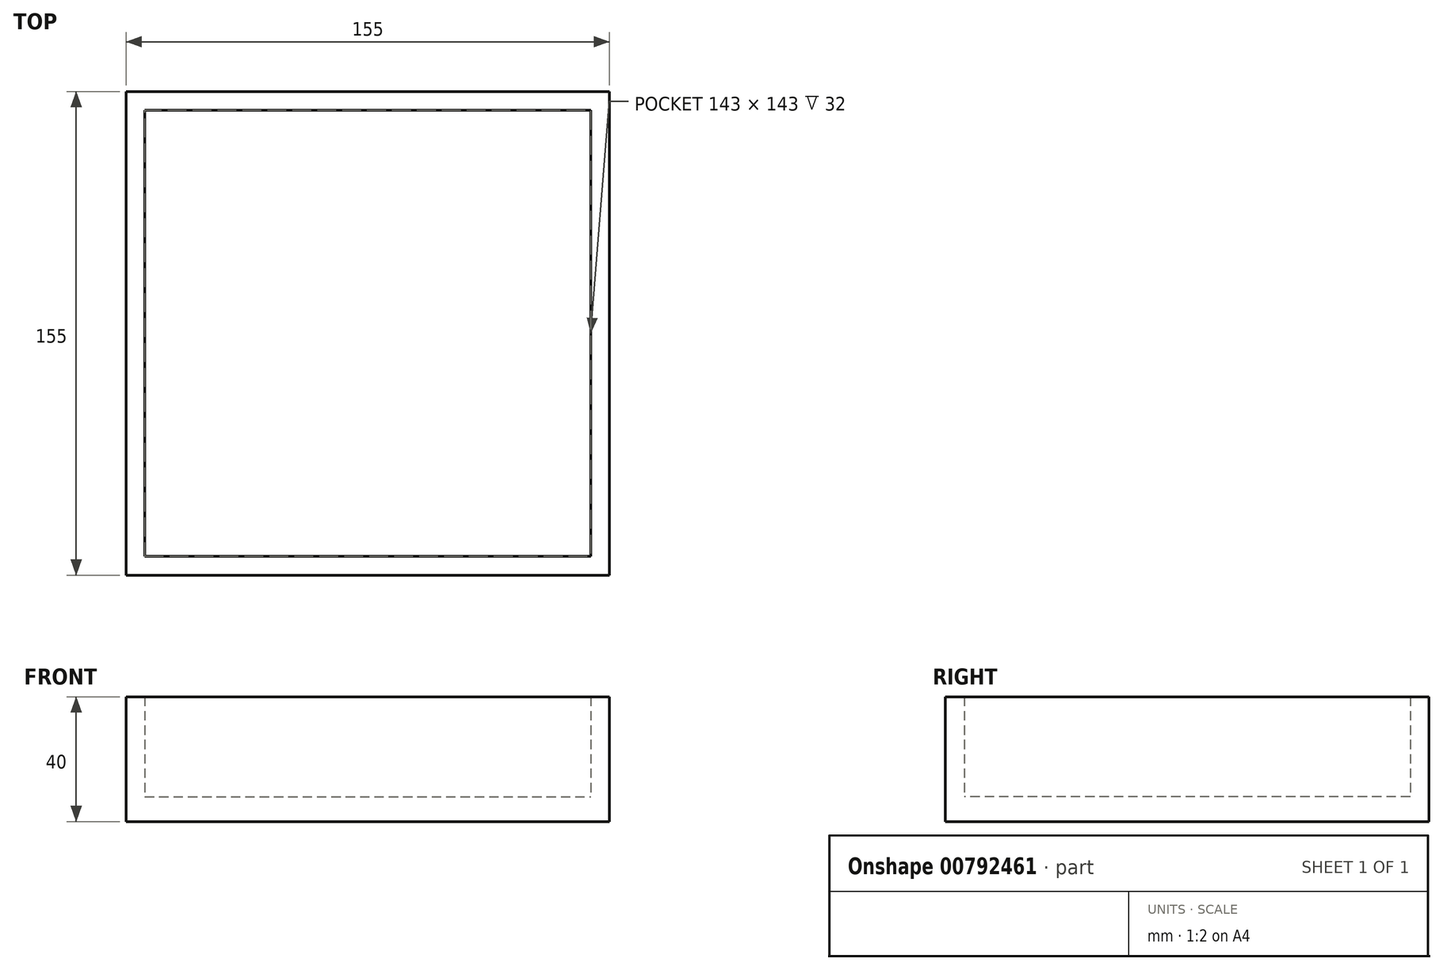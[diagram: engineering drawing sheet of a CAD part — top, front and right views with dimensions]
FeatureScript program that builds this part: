
annotation { "Feature Type Name" : "Feature", "Feature Type Description" : "" }
export const myFeature = defineFeature(function(context is Context, id is Id, definition is map)
    precondition{}
    {
        {
            var Q0;
            Q0=qCreatedBy(makeId("Top.planeOp"),FACE);
            var sketch = newSketch(context, id + "F0", { "sketchPlane" : qUnion([Q0])});
            skLineSegment(sketch, "E0.bottom", {"start": v(-77.5, 77.5) * mm, "end": v(77.5, 77.5) * mm});
            skLineSegment(sketch, "E0.top", {"start": v(-77.5, -77.5) * mm, "end": v(77.5, -77.5) * mm});
            skLineSegment(sketch, "E0.left", {"start": v(-77.5, 77.5) * mm, "end": v(-77.5, -77.5) * mm});
            skLineSegment(sketch, "E0.right", {"start": v(77.5, 77.5) * mm, "end": v(77.5, -77.5) * mm});
            skPoint(sketch, "E0.middle", {"position": v(0, 0) * mm});
            skPoint(sketch, "E1.middle.positionSnap0", {"position": v(-77.5, 0) * mm});
            skPoint(sketch, "E1.centerSnap0", {"position": v(-77.5, 0) * mm});
            skSolve(sketch);
        }
        {
            var Q0;
            Q0=makeQuery(id+"F0.imprint","IMPRINT",FACE,{"disambiguationData":[TD([[makeQuery(id+"F0.imprint","IMPRINT",EDGE,{"derivedFrom":sQuery(id+"F0.wireOp",EDGE,"E0.bottom")}),-1.0]])]});
            extrude(context, id + "F1", {"entities" : qUnion([Q0]), "depth" : 40 * mm, "offsetDistance" : 25 * mm});
        }
        {
            var Q0;
            Q0=makeQuery(id+"F1.opExtrude","CAP_FACE",FACE,{"disambiguationData":[OSD([sQuery(id+"F0.wireOp",EDGE,"E0.bottom"),sQuery(id+"F0.wireOp",EDGE,"E0.top"),sQuery(id+"F0.wireOp",EDGE,"E0.left"),sQuery(id+"F0.wireOp",EDGE,"E0.right")])],"isStart":false});
            shell(context, id + "F2", {"entities" : qUnion([Q0]), "thickness" : 6 * mm});
        }
        {
            var Q0;
            Q0=makeQuery(id+"F2.opShell","OFFSET_FACE",FACE,{"disambiguationData":[OSD([sQuery(id+"F0.wireOp",EDGE,"E0.bottom"),sQuery(id+"F0.wireOp",EDGE,"E0.top"),sQuery(id+"F0.wireOp",EDGE,"E0.left"),sQuery(id+"F0.wireOp",EDGE,"E0.right")])]});
            extrude(context, id + "F3", {"entities" : qUnion([Q0]), "operationType" : NewBodyOperationType.ADD, "depth" : 2 * mm, "offsetDistance" : 25 * mm});
        }
    });
